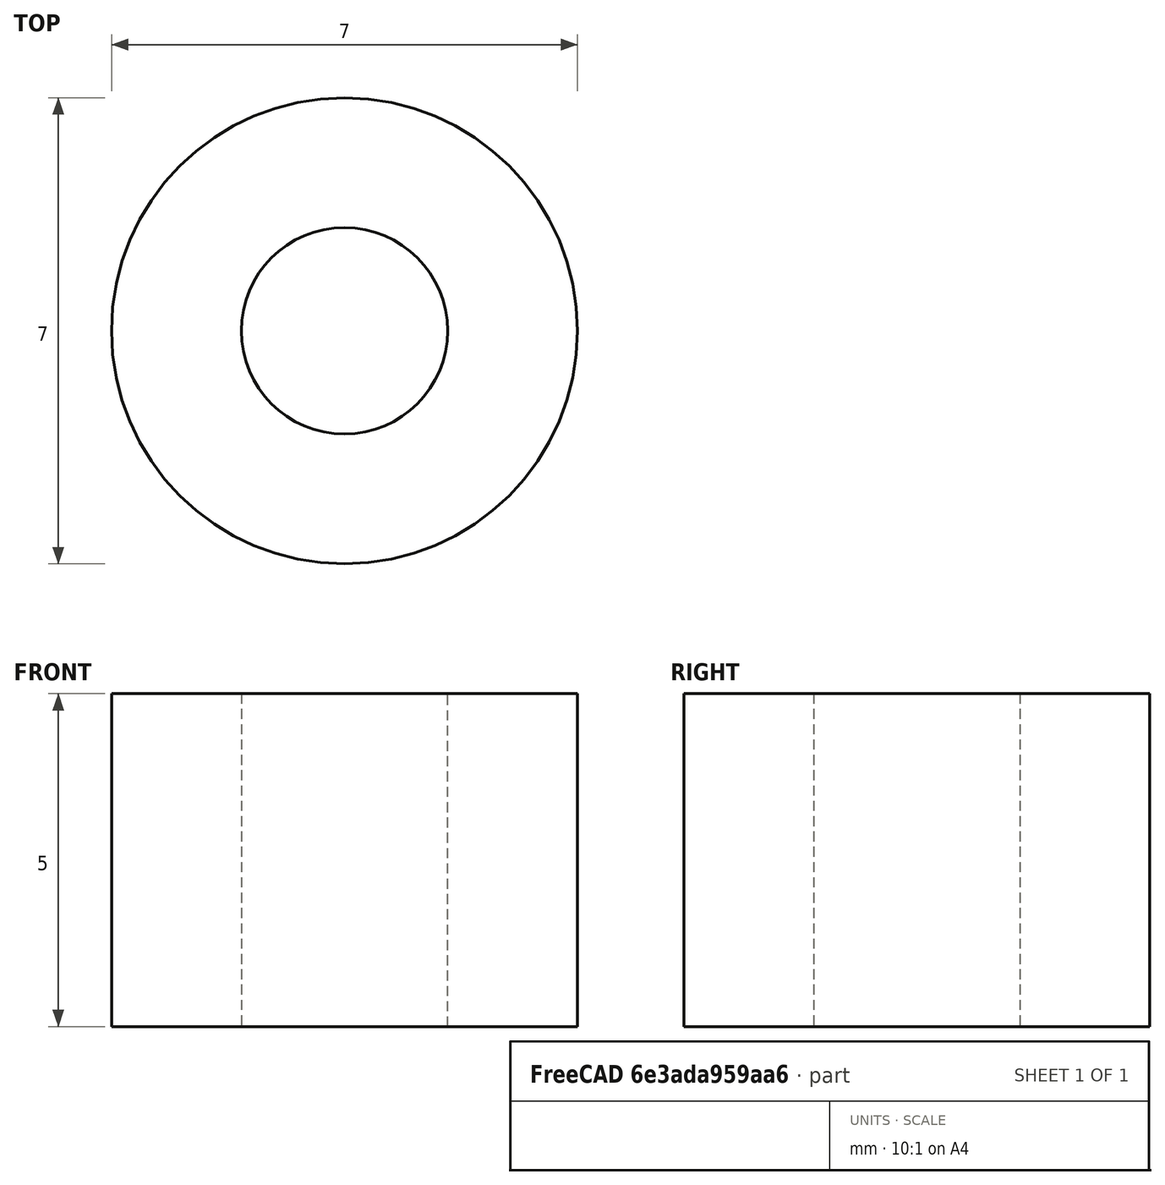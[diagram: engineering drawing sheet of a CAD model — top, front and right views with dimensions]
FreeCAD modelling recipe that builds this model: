
FCSTD DOCUMENT  (FreeCAD 0.20R)
Label: nRF52DK_Spacers
License: All rights reserved
LicenseURL: http://en.wikipedia.org/wiki/All_rights_reserved
objects: Spreadsheet::Sheet×1, Sketcher::SketchObject×1, PartDesign::Pad×1, PartDesign::Body×1
note: 4 computed .brp shape members not serialized (recipe doc carries the construction recipe); baked Part::Feature solids carry a one-line shape summary decoded from their .brp

FEATURE [Spreadsheet::Sheet] Spreadsheet
  cells = A1=Legend; A2=bold; C2=User input (may be changed within some limits); A3=italic; C3=Computed values (do not change); A4=gray background; C4=Fixed input values, e.g. dimensions of PCB & copmonents (don't change unless component was changed); A7=Inner Diameter; B7(inner_diameter)==3.1mm; C7=For M3 screws.; A8=Outer Diameter; B8(outer_diameter)==7mm; A9=Height; B9(height)==5mm
FEATURE [Sketcher::SketchObject] Sketch
  FullyConstrained = true
  MapMode = 5
  Support = -> [XY_Plane]
  expr: Constraints[0] = Spreadsheet.inner_diameter
  expr: Constraints[2] = Spreadsheet.outer_diameter
  sketch-geometry (2):
    g0: Circle CenterX=0 CenterY=0 CenterZ=0 NormalX=0 NormalY=0 NormalZ=1 AngleXU=0 Radius=1.55
    g1: Circle CenterX=0 CenterY=0 CenterZ=0 NormalX=0 NormalY=0 NormalZ=1 AngleXU=0 Radius=3.5
  constraints (4):
    c: Diameter(g0) = 3.1
    c: Coincident(g0,g-1)
    c: Diameter(g1) = 7
    c: Coincident(g1,g0)
FEATURE [PartDesign::Pad] Pad
  Direction = (0,0,1)
  Length = 5
  Length2 = 10
  Profile = -> Sketch
  ReferenceAxis = -> Sketch [N_Axis]
  Type = 0
  expr: Length = Spreadsheet.height
FEATURE [PartDesign::Body] Body
  Group = -> [Sketch,Pad]
  Origin = -> Origin
  Tip = -> Pad
